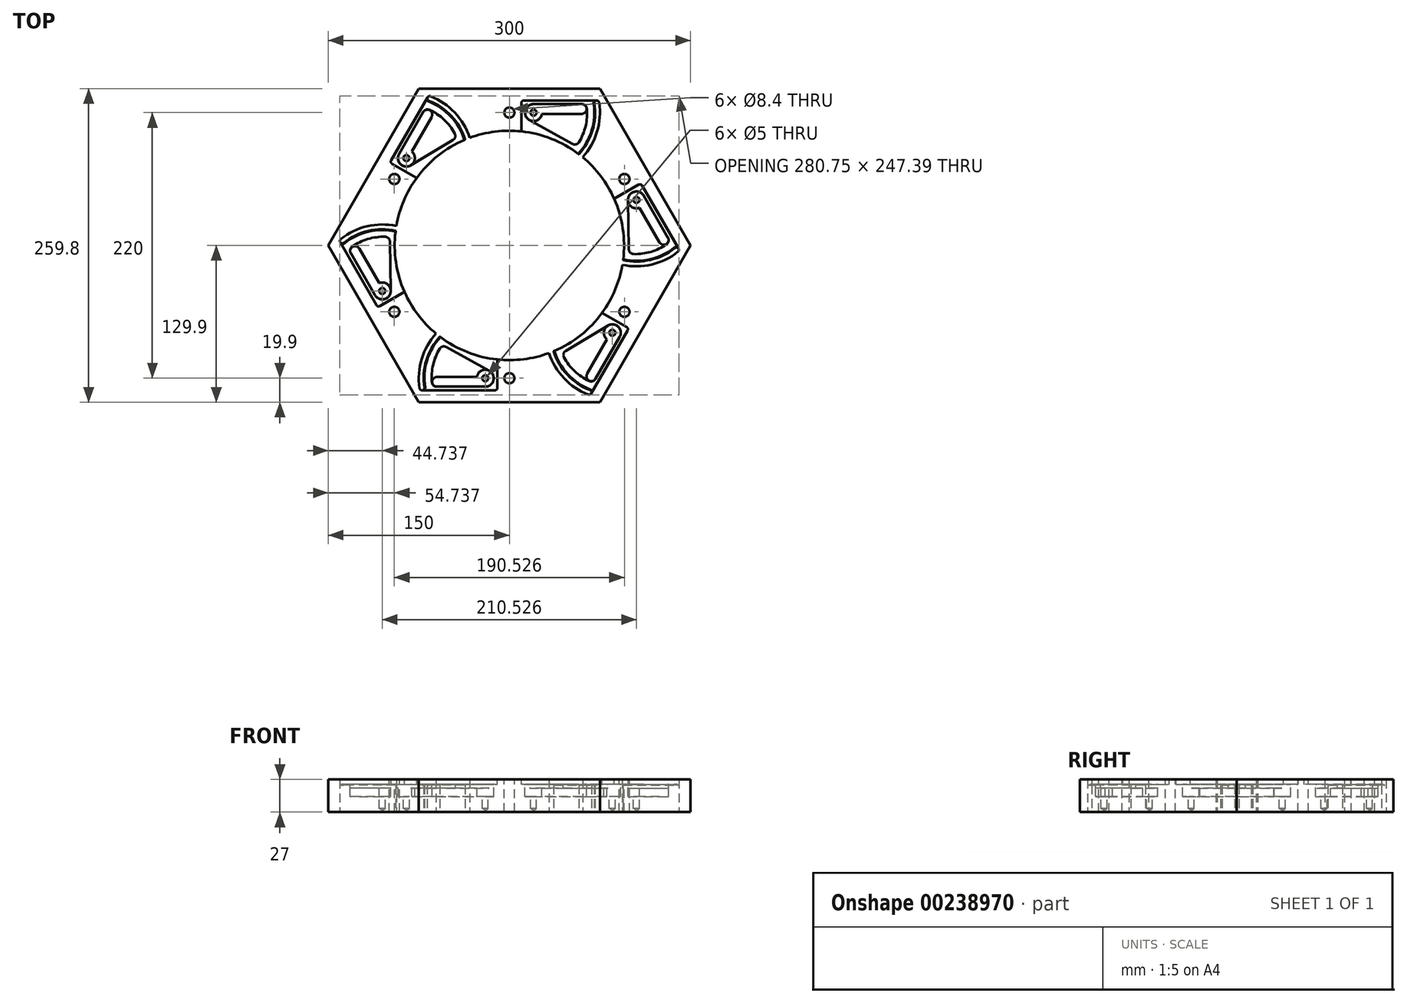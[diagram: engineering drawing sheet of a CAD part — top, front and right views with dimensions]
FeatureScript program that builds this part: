
annotation { "Feature Type Name" : "Feature", "Feature Type Description" : "" }
export const myFeature = defineFeature(function(context is Context, id is Id, definition is map)
    precondition{}
    {
        {
            var Q0;
            Q0=qCreatedBy(makeId("Top.planeOp"),FACE);
            var sketch = newSketch(context, id + "F0", { "sketchPlane" : qUnion([Q0])});
            skCircle(sketch, "E0.cCircle", {"center": v(0, 0) * mm, "radius": 150 * mm, "construction": true});
            skLineSegment(sketch, "E0.0", {"start": v(-75, 129.9) * mm, "end": v(75, 129.9) * mm});
            skLineSegment(sketch, "E0.1", {"start": v(75, 129.9) * mm, "end": v(150, 0) * mm});
            skLineSegment(sketch, "E0.2", {"start": v(150, 0) * mm, "end": v(75, -129.9) * mm});
            skLineSegment(sketch, "E0.3", {"start": v(75, -129.9) * mm, "end": v(-75, -129.9) * mm});
            skLineSegment(sketch, "E0.4", {"start": v(-75, -129.9) * mm, "end": v(-150, 0) * mm});
            skLineSegment(sketch, "E0.5", {"start": v(-150, 0) * mm, "end": v(-75, 129.9) * mm});
            skCircle(sketch, "E1", {"center": v(0, 0) * mm, "radius": 95 * mm});
            skLineSegment(sketch, "E2", {"start": v(0, -192.57) * mm, "end": v(0, 170.24) * mm, "construction": true});
            skCircle(sketch, "E3", {"center": v(0, 0) * mm, "radius": 110 * mm, "construction": true});
            skCircle(sketch, "E4", {"center": v(0, 110) * mm, "radius": 4.2 * mm});
            skCircle(sketch, "E5.1.0", {"center": v(-95.26, 55) * mm, "radius": 4.2 * mm});
            skCircle(sketch, "E5.2.0", {"center": v(-95.26, -55) * mm, "radius": 4.2 * mm});
            skCircle(sketch, "E5.3.0", {"center": v(0, -110) * mm, "radius": 4.2 * mm});
            skCircle(sketch, "E5.4.0", {"center": v(95.26, -55) * mm, "radius": 4.2 * mm});
            skCircle(sketch, "E5.5.0", {"center": v(95.26, 55) * mm, "radius": 4.2 * mm});
            skSolve(sketch);
        }
        {
            var Q0;
            Q0=qSketchRegion(id+"F0",true);
            extrude(context, id + "F1", {"entities" : qUnion([Q0]), "oppositeDirection" : true, "depth" : 25 * mm, "hasSecondDirection" : true, "secondDirectionOppositeDirection" : false, "secondDirectionDepth" : 2 * mm});
        }
        {
            var Q0;
            Q0=qCreatedBy(makeId("Top.planeOp"),FACE);
            var sketch = newSketch(context, id + "F2", { "sketchPlane" : qUnion([Q0])});
            skLineSegment(sketch, "E6", {"start": v(0, 0) * mm, "end": v(-115.33, 66.59) * mm, "construction": true});
            skLineSegment(sketch, "E7", {"start": v(24.73, 8.82) * mm, "end": v(-118.6, 91.57) * mm, "construction": true});
            skLineSegment(sketch, "E8", {"start": v(-73.53, 92.65) * mm, "end": v(-110.35, 28.87) * mm, "construction": true});
            skPoint(sketch, "E9", {"position": v(-85.26, 72.32) * mm});
            skArc(sketch, "E10", {"start": v(-79.2, 122.96) * mm, "mid": v(-97.67, 22.85) * mm, "end": v(-66.72, 119.83) * mm, "construction": true});
            skArc(sketch, "E11", {"start": v(-78.72, 126.93) * mm, "mid": v(-131.29, 42.21) * mm, "end": v(-32.6, 56.43) * mm});
            skCircle(sketch, "E12", {"center": v(-85.26, 72.32) * mm, "radius": 2.5 * mm, "construction": true});
            skArc(sketch, "E13", {"start": v(-86.7, 77.1) * mm, "mid": v(-89.8, 70.21) * mm, "end": v(-82.54, 68.13) * mm, "construction": true});
            skLineSegment(sketch, "E14", {"start": v(-95.36, 62.49) * mm, "end": v(-73.35, 109.7) * mm, "construction": true});
            skArc(sketch, "E15", {"start": v(-86.7, 77.1) * mm, "mid": v(-83.05, 79.12) * mm, "end": v(-80.54, 82.45) * mm, "construction": true});
            skLineSegment(sketch, "E16.trimOffspring", {"start": v(-80.54, 82.45) * mm, "end": v(-62.02, 122.17) * mm, "construction": true});
            skLineSegment(sketch, "E17.trimOffspring", {"start": v(-37.22, 89.44) * mm, "end": v(-33.46, 90.8) * mm});
            skPoint(sketch, "E18", {"position": v(-62.02, 122.17) * mm});
            skPoint(sketch, "E19", {"position": v(-33.46, 90.8) * mm});
            skArc(sketch, "E20", {"start": v(-37.22, 89.44) * mm, "mid": v(-37.91, 91.27) * mm, "end": v(-38.67, 93.07) * mm});
            skLineSegment(sketch, "E21", {"start": v(-82.54, 68.13) * mm, "end": v(-42.49, 94.14) * mm, "construction": true});
            skLineSegment(sketch, "E22", {"start": v(-50.7, 85.23) * mm, "end": v(-31.42, 97.75) * mm, "construction": true});
            skPoint(sketch, "E23", {"position": v(-39.97, 95.77) * mm});
            skCircle(sketch, "E24", {"center": v(-39.97, 95.77) * mm, "radius": 3 * mm, "construction": true});
            skPoint(sketch, "E25", {"position": v(-42.49, 94.14) * mm});
            skArc(sketch, "E26.trimOffspring", {"start": v(-39.97, 95.77) * mm, "mid": v(-49.96, 109.12) * mm, "end": v(-63.7, 118.54) * mm, "construction": true});
            skLineSegment(sketch, "E27.trimOffspring", {"start": v(-39.97, 95.77) * mm, "end": v(-16, 111.34) * mm});
            skArc(sketch, "E28", {"start": v(-38.67, 93.07) * mm, "mid": v(-40.33, 94.5) * mm, "end": v(-42.49, 94.14) * mm});
            skPoint(sketch, "E29", {"position": v(-77.2, 132.91) * mm});
            skPoint(sketch, "E30", {"position": v(-78.72, 126.93) * mm});
            skLineSegment(sketch, "E31", {"start": v(-85.26, 72.32) * mm, "end": v(-78.72, 126.93) * mm, "construction": true});
            skLineSegment(sketch, "E32", {"start": v(-85.21, 72.2) * mm, "end": v(-33.46, 90.8) * mm, "construction": true});
            skPoint(sketch, "E33", {"position": v(-56.33, 130.09) * mm});
            skLineSegment(sketch, "E34", {"start": v(-97.92, 70.4) * mm, "end": v(-67.73, 122.7) * mm});
            skLineSegment(sketch, "E35.1.0", {"start": v(0, 0) * mm, "end": v(-115.33, -66.59) * mm});
            skPoint(sketch, "E35.1.1", {"position": v(-105.26, -37.68) * mm});
            skLineSegment(sketch, "E35.2.0", {"start": v(0, 0) * mm, "end": v(0, -133.17) * mm});
            skPoint(sketch, "E35.2.1", {"position": v(-20, -110) * mm});
            skLineSegment(sketch, "E35.3.0", {"start": v(0, 0) * mm, "end": v(115.33, -66.59) * mm});
            skPoint(sketch, "E35.3.1", {"position": v(85.26, -72.32) * mm});
            skLineSegment(sketch, "E35.4.0", {"start": v(0, 0) * mm, "end": v(115.33, 66.59) * mm});
            skPoint(sketch, "E35.4.1", {"position": v(105.26, 37.68) * mm});
            skLineSegment(sketch, "E35.5.0", {"start": v(0, 0) * mm, "end": v(0, 133.17) * mm});
            skPoint(sketch, "E35.5.1", {"position": v(20, 110) * mm});
            skPoint(sketch, "E35.center", {"position": v(0, 0) * mm});
            skCircle(sketch, "E36.0", {"center": v(0, 0) * mm, "radius": 95 * mm, "construction": true});
            skPoint(sketch, "E37", {"position": v(-32.9, 89.12) * mm});
            skLineSegment(sketch, "E38", {"start": v(-32.9, 89.12) * mm, "end": v(32.9, -89.12) * mm, "construction": true});
            skPoint(sketch, "E39", {"position": v(-22.5, 60.98) * mm});
            skPoint(sketch, "E40", {"position": v(5.2, -14.07) * mm});
            skCircle(sketch, "E41", {"center": v(5.2, -14.07) * mm, "radius": 80 * mm, "construction": true});
            skArc(sketch, "E42.filletArc", {"start": v(-65.27, 123.56) * mm, "mid": v(-66.66, 123.58) * mm, "end": v(-67.73, 122.7) * mm});
            skLineSegment(sketch, "E43", {"start": v(-32.6, 56.43) * mm, "end": v(-85.26, 72.32) * mm, "construction": true});
            skLineSegment(sketch, "E44", {"start": v(-76.12, 72.3) * mm, "end": v(-85.21, 72.2) * mm});
            skLineSegment(sketch, "E45", {"start": v(-85.21, 72.2) * mm, "end": v(-56.33, 90.95) * mm, "construction": true});
            skLineSegment(sketch, "E46", {"start": v(-85.21, 72.2) * mm, "end": v(-48.78, 69.91) * mm, "construction": true});
            skLineSegment(sketch, "E47", {"start": v(-48.77, 65.04) * mm, "end": v(-92.23, 67.76) * mm, "construction": true});
            skCircle(sketch, "E48", {"center": v(-85.21, 72.2) * mm, "radius": 10 * mm, "construction": true});
            skLineSegment(sketch, "E49", {"start": v(-87.5, 62.45) * mm, "end": v(-55.32, 60.44) * mm, "construction": true});
            skLineSegment(sketch, "E50", {"start": v(-97.2, 67.66) * mm, "end": v(-68.1, 50.87) * mm});
            skArc(sketch, "E51.filletArc", {"start": v(-97.92, 70.4) * mm, "mid": v(-98.12, 68.87) * mm, "end": v(-97.2, 67.66) * mm});
            skArc(sketch, "E52", {"start": v(-67.73, 122.7) * mm, "mid": v(-67.88, 121.03) * mm, "end": v(-66.72, 119.83) * mm, "construction": true});
            skArc(sketch, "E53.converted", {"start": v(-30.7, 79.26) * mm, "mid": v(-41.9, 106.16) * mm, "end": v(-65.27, 123.56) * mm});
            skArc(sketch, "E54", {"start": v(-30.7, 79.26) * mm, "mid": v(-51.4, 67.7) * mm, "end": v(-68.1, 50.87) * mm});
            skLineSegment(sketch, "E55.trimOffspring", {"start": v(-52.18, 41.68) * mm, "end": v(-31.82, 29.92) * mm});
            skSolve(sketch);
        }
        {
            var Q0;
            Q0=qCreatedBy(makeId("Front.planeOp"),FACE);
            var sketch = newSketch(context, id + "F3", { "sketchPlane" : qUnion([Q0])});
            skLineSegment(sketch, "E56", {"start": v(0, -93.36) * mm, "end": v(0, 93) * mm, "construction": true});
            skSolve(sketch);
        }
        {
            var Q0;
            Q0=qSketchRegion(id+"F2",true);
            extrude(context, id + "F4", {"entities" : qUnion([Q0]), "depth" : 25 * mm, "hasSecondDirection" : true, "secondDirectionOppositeDirection" : true, "secondDirectionDepth" : 2.1 * mm});
        }
        {
            var Q0;
            Q0=makeQuery(id+"F4.opExtrude","SWEPT_BODY",BODY,{"disambiguationData":[OSD([sQuery(id+"F2.wireOp",EDGE,"E34"),sQuery(id+"F2.wireOp",EDGE,"E42.filletArc"),sQuery(id+"F2.wireOp",EDGE,"E50"),sQuery(id+"F2.wireOp",EDGE,"E51.filletArc"),sQuery(id+"F2.wireOp",EDGE,"E54"),sQuery(id+"F2.wireOp",EDGE,"E53.converted")])]});
            var Q1;
            Q1=sQuery(id+"F3.wireOp",EDGE,"E56");
            circularPattern(context, id + "F5", {"entities" : qUnion([Q0]), "axis" : qUnion([Q1]), "angle" : 360 * degree, "instanceCount" : 6, "equalSpace" : true});
        }
        {
            var Q0;
            Q0=makeQuery(id+"F5.opPattern","COPY",BODY,{"derivedFrom":makeQuery(id+"F4.opExtrude","SWEPT_BODY",BODY,{"disambiguationData":[OSD([sQuery(id+"F2.wireOp",EDGE,"E34"),sQuery(id+"F2.wireOp",EDGE,"E42.filletArc"),sQuery(id+"F2.wireOp",EDGE,"E50"),sQuery(id+"F2.wireOp",EDGE,"E51.filletArc"),sQuery(id+"F2.wireOp",EDGE,"E54"),sQuery(id+"F2.wireOp",EDGE,"E53.converted")])]}),"instanceName":"1"});
            var Q1;
            Q1=makeQuery(id+"F4.opExtrude","SWEPT_BODY",BODY,{"disambiguationData":[OSD([sQuery(id+"F2.wireOp",EDGE,"E34"),sQuery(id+"F2.wireOp",EDGE,"E42.filletArc"),sQuery(id+"F2.wireOp",EDGE,"E50"),sQuery(id+"F2.wireOp",EDGE,"E51.filletArc"),sQuery(id+"F2.wireOp",EDGE,"E54"),sQuery(id+"F2.wireOp",EDGE,"E53.converted")])]});
            var Q2;
            Q2=makeQuery(id+"F5.opPattern","COPY",BODY,{"derivedFrom":makeQuery(id+"F4.opExtrude","SWEPT_BODY",BODY,{"disambiguationData":[OSD([sQuery(id+"F2.wireOp",EDGE,"E34"),sQuery(id+"F2.wireOp",EDGE,"E42.filletArc"),sQuery(id+"F2.wireOp",EDGE,"E50"),sQuery(id+"F2.wireOp",EDGE,"E51.filletArc"),sQuery(id+"F2.wireOp",EDGE,"E54"),sQuery(id+"F2.wireOp",EDGE,"E53.converted")])]}),"instanceName":"5"});
            var Q3;
            Q3=makeQuery(id+"F5.opPattern","COPY",BODY,{"derivedFrom":makeQuery(id+"F4.opExtrude","SWEPT_BODY",BODY,{"disambiguationData":[OSD([sQuery(id+"F2.wireOp",EDGE,"E34"),sQuery(id+"F2.wireOp",EDGE,"E42.filletArc"),sQuery(id+"F2.wireOp",EDGE,"E50"),sQuery(id+"F2.wireOp",EDGE,"E51.filletArc"),sQuery(id+"F2.wireOp",EDGE,"E54"),sQuery(id+"F2.wireOp",EDGE,"E53.converted")])]}),"instanceName":"4"});
            var Q4;
            Q4=makeQuery(id+"F5.opPattern","COPY",BODY,{"derivedFrom":makeQuery(id+"F4.opExtrude","SWEPT_BODY",BODY,{"disambiguationData":[OSD([sQuery(id+"F2.wireOp",EDGE,"E34"),sQuery(id+"F2.wireOp",EDGE,"E42.filletArc"),sQuery(id+"F2.wireOp",EDGE,"E50"),sQuery(id+"F2.wireOp",EDGE,"E51.filletArc"),sQuery(id+"F2.wireOp",EDGE,"E54"),sQuery(id+"F2.wireOp",EDGE,"E53.converted")])]}),"instanceName":"3"});
            var Q5;
            Q5=makeQuery(id+"F5.opPattern","COPY",BODY,{"derivedFrom":makeQuery(id+"F4.opExtrude","SWEPT_BODY",BODY,{"disambiguationData":[OSD([sQuery(id+"F2.wireOp",EDGE,"E34"),sQuery(id+"F2.wireOp",EDGE,"E42.filletArc"),sQuery(id+"F2.wireOp",EDGE,"E50"),sQuery(id+"F2.wireOp",EDGE,"E51.filletArc"),sQuery(id+"F2.wireOp",EDGE,"E54"),sQuery(id+"F2.wireOp",EDGE,"E53.converted")])]}),"instanceName":"2"});
            var Q6;
            Q6=makeQuery(id+"F1.opExtrude","SWEPT_BODY",BODY,{"disambiguationData":[OSD([sQuery(id+"F0.wireOp",EDGE,"E0.0"),sQuery(id+"F0.wireOp",EDGE,"E0.1"),sQuery(id+"F0.wireOp",EDGE,"E0.2"),sQuery(id+"F0.wireOp",EDGE,"E0.3"),sQuery(id+"F0.wireOp",EDGE,"E0.4"),sQuery(id+"F0.wireOp",EDGE,"E0.5"),sQuery(id+"F0.wireOp",EDGE,"E1")])]});
            booleanBodies(context, id + "F6", {"operationType" : BooleanOperationType.SUBTRACTION, "tools" : qUnion([Q0, Q1, Q2, Q3, Q4, Q5]), "targets" : qUnion([Q6])});
        }
        {
            var Q0;
            Q0=makeQuery(id+"F0.imprint","IMPRINT",FACE,{"disambiguationData":[TD([[makeQuery(id+"F0.imprint","IMPRINT",EDGE,{"derivedFrom":sQuery(id+"F0.wireOp",EDGE,"E1")}),1.0]])]});
            var sketch = newSketch(context, id + "F7", { "sketchPlane" : qUnion([Q0])});
            skArc(sketch, "E57.1", {"start": v(-34.54, 77.66) * mm, "mid": v(-44.72, 103.26) * mm, "end": v(-66.72, 119.83) * mm});
            skArc(sketch, "E58.0", {"start": v(-30.7, 79.26) * mm, "mid": v(-32.63, 78.49) * mm, "end": v(-34.54, 77.66) * mm});
            skArc(sketch, "E59.0", {"start": v(-67.73, 122.7) * mm, "mid": v(-67.88, 121.03) * mm, "end": v(-66.72, 119.83) * mm});
            skArc(sketch, "E59.1", {"start": v(-65.27, 123.56) * mm, "mid": v(-66.66, 123.58) * mm, "end": v(-67.73, 122.7) * mm});
            skArc(sketch, "E59.2", {"start": v(-30.7, 79.26) * mm, "mid": v(-41.9, 106.16) * mm, "end": v(-65.27, 123.56) * mm});
            skPoint(sketch, "E60.orphan", {"position": v(-68.1, 50.87) * mm});
            skPoint(sketch, "E61.orphan", {"position": v(-79.2, 122.96) * mm});
            skPoint(sketch, "E57.0.end.orphan", {"position": v(-97.92, 70.4) * mm});
            skPoint(sketch, "E57.0.start.orphan", {"position": v(-67.73, 122.7) * mm});
            skSolve(sketch);
        }
        {
            var Q0;
            Q0=qSketchRegion(id+"F7",true);
            extrude(context, id + "F8", {"entities" : qUnion([Q0]), "depth" : 10 * mm, "hasSecondDirection" : true, "secondDirectionOppositeDirection" : true, "secondDirectionDepth" : 35 * mm});
        }
        {
            var Q0;
            Q0=makeQuery(id+"F8.opExtrude","SWEPT_BODY",BODY,{"disambiguationData":[OSD([sQuery(id+"F7.wireOp",EDGE,"E57.1"),sQuery(id+"F7.wireOp",EDGE,"E58.0"),sQuery(id+"F7.wireOp",EDGE,"E59.0"),sQuery(id+"F7.wireOp",EDGE,"E59.1"),sQuery(id+"F7.wireOp",EDGE,"E59.2")])]});
            var Q1;
            Q1=sQuery(id+"F3.wireOp",EDGE,"E56");
            circularPattern(context, id + "F9", {"entities" : qUnion([Q0]), "axis" : qUnion([Q1]), "angle" : 360 * degree, "instanceCount" : 6, "equalSpace" : true});
        }
        {
            var Q0;
            Q0=makeQuery(id+"F8.opExtrude","SWEPT_BODY",BODY,{"disambiguationData":[OSD([sQuery(id+"F7.wireOp",EDGE,"E57.1"),sQuery(id+"F7.wireOp",EDGE,"E58.0"),sQuery(id+"F7.wireOp",EDGE,"E59.0"),sQuery(id+"F7.wireOp",EDGE,"E59.1"),sQuery(id+"F7.wireOp",EDGE,"E59.2")])]});
            var Q1;
            Q1=makeQuery(id+"F9.opPattern","COPY",BODY,{"derivedFrom":makeQuery(id+"F8.opExtrude","SWEPT_BODY",BODY,{"disambiguationData":[OSD([sQuery(id+"F7.wireOp",EDGE,"E57.1"),sQuery(id+"F7.wireOp",EDGE,"E58.0"),sQuery(id+"F7.wireOp",EDGE,"E59.0"),sQuery(id+"F7.wireOp",EDGE,"E59.1"),sQuery(id+"F7.wireOp",EDGE,"E59.2")])]}),"instanceName":"5"});
            var Q2;
            Q2=makeQuery(id+"F9.opPattern","COPY",BODY,{"derivedFrom":makeQuery(id+"F8.opExtrude","SWEPT_BODY",BODY,{"disambiguationData":[OSD([sQuery(id+"F7.wireOp",EDGE,"E57.1"),sQuery(id+"F7.wireOp",EDGE,"E58.0"),sQuery(id+"F7.wireOp",EDGE,"E59.0"),sQuery(id+"F7.wireOp",EDGE,"E59.1"),sQuery(id+"F7.wireOp",EDGE,"E59.2")])]}),"instanceName":"4"});
            var Q3;
            Q3=makeQuery(id+"F9.opPattern","COPY",BODY,{"derivedFrom":makeQuery(id+"F8.opExtrude","SWEPT_BODY",BODY,{"disambiguationData":[OSD([sQuery(id+"F7.wireOp",EDGE,"E57.1"),sQuery(id+"F7.wireOp",EDGE,"E58.0"),sQuery(id+"F7.wireOp",EDGE,"E59.0"),sQuery(id+"F7.wireOp",EDGE,"E59.1"),sQuery(id+"F7.wireOp",EDGE,"E59.2")])]}),"instanceName":"3"});
            var Q4;
            Q4=makeQuery(id+"F9.opPattern","COPY",BODY,{"derivedFrom":makeQuery(id+"F8.opExtrude","SWEPT_BODY",BODY,{"disambiguationData":[OSD([sQuery(id+"F7.wireOp",EDGE,"E57.1"),sQuery(id+"F7.wireOp",EDGE,"E58.0"),sQuery(id+"F7.wireOp",EDGE,"E59.0"),sQuery(id+"F7.wireOp",EDGE,"E59.1"),sQuery(id+"F7.wireOp",EDGE,"E59.2")])]}),"instanceName":"2"});
            var Q5;
            Q5=makeQuery(id+"F9.opPattern","COPY",BODY,{"derivedFrom":makeQuery(id+"F8.opExtrude","SWEPT_BODY",BODY,{"disambiguationData":[OSD([sQuery(id+"F7.wireOp",EDGE,"E57.1"),sQuery(id+"F7.wireOp",EDGE,"E58.0"),sQuery(id+"F7.wireOp",EDGE,"E59.0"),sQuery(id+"F7.wireOp",EDGE,"E59.1"),sQuery(id+"F7.wireOp",EDGE,"E59.2")])]}),"instanceName":"1"});
            var Q6;
            Q6=makeQuery(id+"F1.opExtrude","SWEPT_BODY",BODY,{"disambiguationData":[OSD([sQuery(id+"F0.wireOp",EDGE,"E0.0"),sQuery(id+"F0.wireOp",EDGE,"E0.1"),sQuery(id+"F0.wireOp",EDGE,"E0.2"),sQuery(id+"F0.wireOp",EDGE,"E0.3"),sQuery(id+"F0.wireOp",EDGE,"E0.4"),sQuery(id+"F0.wireOp",EDGE,"E0.5"),sQuery(id+"F0.wireOp",EDGE,"E1")])]});
            booleanBodies(context, id + "F10", {"operationType" : BooleanOperationType.SUBTRACTION, "tools" : qUnion([Q0, Q1, Q2, Q3, Q4, Q5]), "targets" : qUnion([Q6])});
        }
        {
            var Q0;
            Q0=sQuery(id+"F2.wireOp",VERTEX,"E35.5.1");
            var Q1;
            Q1=sQuery(id+"F2.wireOp",VERTEX,"E35.4.1");
            var Q2;
            Q2=sQuery(id+"F2.wireOp",VERTEX,"E35.3.1");
            var Q3;
            Q3=sQuery(id+"F2.wireOp",VERTEX,"E35.2.1");
            var Q4;
            Q4=sQuery(id+"F2.wireOp",VERTEX,"E35.1.1");
            var Q5;
            Q5=sQuery(id+"F2.wireOp",VERTEX,"E9");
            var Q6;
            Q6=makeQuery(id+"F1.opExtrude","SWEPT_BODY",BODY,{"disambiguationData":[OSD([sQuery(id+"F0.wireOp",EDGE,"E0.0"),sQuery(id+"F0.wireOp",EDGE,"E0.1"),sQuery(id+"F0.wireOp",EDGE,"E0.2"),sQuery(id+"F0.wireOp",EDGE,"E0.3"),sQuery(id+"F0.wireOp",EDGE,"E0.4"),sQuery(id+"F0.wireOp",EDGE,"E0.5"),sQuery(id+"F0.wireOp",EDGE,"E1")])]});
            hole(context, id + "F11", {"style" : HoleStyle.SIMPLE, "endStyle" : HoleEndStyle.BLIND, "holeDiameter" : 5 * mm, "holeDepth" : 20 * mm, "locations" : qUnion([Q0, Q1, Q2, Q3, Q4, Q5]), "scope" : qUnion([Q6])});
        }
        {
            var Q0;
            Q0=makeQuery(id+"F6.opBoolean","COPY",FACE,{"derivedFrom":makeQuery(id+"F4.opExtrude","CAP_FACE",FACE,{"disambiguationData":[OSD([sQuery(id+"F2.wireOp",EDGE,"E34"),sQuery(id+"F2.wireOp",EDGE,"E42.filletArc"),sQuery(id+"F2.wireOp",EDGE,"E50"),sQuery(id+"F2.wireOp",EDGE,"E51.filletArc"),sQuery(id+"F2.wireOp",EDGE,"E54"),sQuery(id+"F2.wireOp",EDGE,"E53.converted")])],"isStart":true})});
            cPlane(context, id + "F12", {"entities" : qUnion([Q0]), "cplaneType" : CPlaneType.OFFSET, "offset" : 0 * mm, "width" : 150 * mm, "height" : 150 * mm});
        }
        {
            var Q0;
            Q0=qCreatedBy(id+"F12.planeOp",FACE);
            var sketch = newSketch(context, id + "F13", { "sketchPlane" : qUnion([Q0])});
            skCircle(sketch, "E62.0", {"center": v(-85.26, 72.32) * mm, "radius": 7 * mm});
            skLineSegment(sketch, "E63", {"start": v(-91.32, 75.82) * mm, "end": v(-67.64, 116.85) * mm});
            skLineSegment(sketch, "E64", {"start": v(-87.86, 73.82) * mm, "end": v(-63.58, 115.87) * mm, "construction": true});
            skLineSegment(sketch, "E65", {"start": v(-91.32, 75.82) * mm, "end": v(-76.61, 67.33) * mm, "construction": true});
            skLineSegment(sketch, "E66", {"start": v(-77.1, 113.8) * mm, "end": v(-55.5, 101.33) * mm, "construction": true});
            skArc(sketch, "E67", {"start": v(-64.4, 106.46) * mm, "mid": v(-65.86, 111.93) * mm, "end": v(-71.32, 110.46) * mm});
            skArc(sketch, "E68", {"start": v(-91.32, 75.82) * mm, "mid": v(-89.86, 70.36) * mm, "end": v(-84.4, 71.82) * mm});
            skLineSegment(sketch, "E69", {"start": v(-64.4, 106.46) * mm, "end": v(-84.4, 71.82) * mm});
            skSolve(sketch);
        }
        {
            var Q0;
            Q0 = qSketchRegion(id + "F13", true);
            extrude(context, id + "F14", {"entities" : qUnion([Q0]), "oppositeDirection" : true, "depth" : 10 * mm, "hasSecondDirection" : true, "secondDirectionOppositeDirection" : false, "secondDirectionDepth" : 25 * mm});
        }
        {
            var Q0;
            Q0=makeQuery(id+"F14.opExtrude","SWEPT_BODY",BODY,{"disambiguationData":[OSD([sQuery(id+"F13.wireOp",EDGE,"E62.0")])]});
            var Q1;
            Q1=sQuery(id+"F3.wireOp",EDGE,"E56");
            circularPattern(context, id + "F15", {"operationType" : NewBodyOperationType.REMOVE, "entities" : qUnion([Q0]), "axis" : qUnion([Q1]), "angle" : 360 * degree, "instanceCount" : 6, "equalSpace" : true});
        }
        {
            var Q0;
            Q0=qCreatedBy(id+"F12.planeOp",FACE);
            var sketch = newSketch(context, id + "F16", { "sketchPlane" : qUnion([Q0])});
            skArc(sketch, "E70.0", {"start": v(-66.31, 118.88) * mm, "mid": v(-47.6, 106.21) * mm, "end": v(-36.21, 86.7) * mm, "construction": true});
            skCircle(sketch, "E71.0", {"center": v(-85.26, 72.32) * mm, "radius": 4.5 * mm, "construction": true});
            skLineSegment(sketch, "E72.0", {"start": v(-67.73, 122.7) * mm, "end": v(-103.72, 60.35) * mm, "construction": true});
            skArc(sketch, "E73.0", {"start": v(-76.82, 55.9) * mm, "mid": v(-58.9, 74.54) * mm, "end": v(-36.62, 87.66) * mm, "construction": true});
            skArc(sketch, "E74", {"start": v(-45.23, 92.65) * mm, "mid": v(-54.06, 104.16) * mm, "end": v(-66.1, 112.27) * mm});
            skPoint(sketch, "E75.orphan", {"position": v(-61.95, 122.7) * mm});
            skArc(sketch, "E76.0.0", {"start": v(-91.32, 75.82) * mm, "mid": v(-90.17, 67.33) * mm, "end": v(-81.66, 66.32) * mm});
            skLineSegment(sketch, "E77", {"start": v(-91.32, 75.82) * mm, "end": v(-71.23, 110.63) * mm});
            skLineSegment(sketch, "E78", {"start": v(-46.7, 87.33) * mm, "end": v(-81.66, 66.32) * mm});
            skPoint(sketch, "E79.visualSharp", {"position": v(-69.48, 113.66) * mm});
            skArc(sketch, "E79.filletArc", {"start": v(-66.1, 112.27) * mm, "mid": v(-68.97, 112.45) * mm, "end": v(-71.23, 110.63) * mm});
            skPoint(sketch, "E80.visualSharp", {"position": v(-43.57, 89.2) * mm});
            skArc(sketch, "E80.filletArc", {"start": v(-46.7, 87.33) * mm, "mid": v(-44.9, 89.7) * mm, "end": v(-45.23, 92.65) * mm});
            skSolve(sketch);
        }
        {
            var Q0;
            Q0 = qSketchRegion(id + "F16", true);
            extrude(context, id + "F17", {"entities" : qUnion([Q0]), "oppositeDirection" : true, "depth" : 3 * mm, "hasSecondDirection" : true, "secondDirectionOppositeDirection" : false, "secondDirectionDepth" : 25 * mm});
        }
        {
            var Q0;
            Q0=makeQuery(id+"F17.opExtrude","SWEPT_BODY",BODY,{"disambiguationData":[OSD([sQuery(id+"F16.wireOp",EDGE,"E74"),sQuery(id+"F16.wireOp",EDGE,"E76.0.0"),sQuery(id+"F16.wireOp",EDGE,"E77"),sQuery(id+"F16.wireOp",EDGE,"E78"),sQuery(id+"F16.wireOp",EDGE,"E79.filletArc"),sQuery(id+"F16.wireOp",EDGE,"E80.filletArc")])]});
            var Q1;
            Q1=sQuery(id+"F3.wireOp",EDGE,"E56");
            circularPattern(context, id + "F18", {"operationType" : NewBodyOperationType.REMOVE, "entities" : qUnion([Q0]), "axis" : qUnion([Q1]), "angle" : 360 * degree, "instanceCount" : 6, "oppositeDirection" : true, "equalSpace" : true});
        }
        {
            var Q0;
            Q0=makeQuery(id+"F10.opBoolean","INTERSECT",EDGE,{"derivedFrom":[makeQuery(id+"F6.opBoolean","COPY",FACE,{"derivedFrom":makeQuery(id+"F5.opPattern","COPY",FACE,{"derivedFrom":makeQuery(id+"F4.opExtrude","CAP_FACE",FACE,{"disambiguationData":[OSD([sQuery(id+"F2.wireOp",EDGE,"E34"),sQuery(id+"F2.wireOp",EDGE,"E42.filletArc"),sQuery(id+"F2.wireOp",EDGE,"E50"),sQuery(id+"F2.wireOp",EDGE,"E51.filletArc"),sQuery(id+"F2.wireOp",EDGE,"E54"),sQuery(id+"F2.wireOp",EDGE,"E53.converted")])],"isStart":true}),"instanceName":"1"})}),makeQuery(id+"F9.opPattern","COPY",FACE,{"derivedFrom":makeQuery(id+"F8.opExtrude","SWEPT_FACE",FACE,{"disambiguationData":[OSD([sQuery(id+"F7.wireOp",EDGE,"E57.1")])]}),"instanceName":"1"})]});
            var Q1;
            Q1=makeQuery(id+"F10.opBoolean","INTERSECT",EDGE,{"derivedFrom":[makeQuery(id+"F6.opBoolean","COPY",FACE,{"derivedFrom":makeQuery(id+"F4.opExtrude","CAP_FACE",FACE,{"disambiguationData":[OSD([sQuery(id+"F2.wireOp",EDGE,"E34"),sQuery(id+"F2.wireOp",EDGE,"E42.filletArc"),sQuery(id+"F2.wireOp",EDGE,"E50"),sQuery(id+"F2.wireOp",EDGE,"E51.filletArc"),sQuery(id+"F2.wireOp",EDGE,"E54"),sQuery(id+"F2.wireOp",EDGE,"E53.converted")])],"isStart":true})}),makeQuery(id+"F8.opExtrude","SWEPT_FACE",FACE,{"disambiguationData":[OSD([sQuery(id+"F7.wireOp",EDGE,"E57.1")])]})]});
            var Q2;
            Q2=makeQuery(id+"F10.opBoolean","INTERSECT",EDGE,{"derivedFrom":[makeQuery(id+"F6.opBoolean","COPY",FACE,{"derivedFrom":makeQuery(id+"F5.opPattern","COPY",FACE,{"derivedFrom":makeQuery(id+"F4.opExtrude","CAP_FACE",FACE,{"disambiguationData":[OSD([sQuery(id+"F2.wireOp",EDGE,"E34"),sQuery(id+"F2.wireOp",EDGE,"E42.filletArc"),sQuery(id+"F2.wireOp",EDGE,"E50"),sQuery(id+"F2.wireOp",EDGE,"E51.filletArc"),sQuery(id+"F2.wireOp",EDGE,"E54"),sQuery(id+"F2.wireOp",EDGE,"E53.converted")])],"isStart":true}),"instanceName":"5"})}),makeQuery(id+"F9.opPattern","COPY",FACE,{"derivedFrom":makeQuery(id+"F8.opExtrude","SWEPT_FACE",FACE,{"disambiguationData":[OSD([sQuery(id+"F7.wireOp",EDGE,"E57.1")])]}),"instanceName":"5"})]});
            var Q3;
            Q3=makeQuery(id+"F10.opBoolean","INTERSECT",EDGE,{"derivedFrom":[makeQuery(id+"F6.opBoolean","COPY",FACE,{"derivedFrom":makeQuery(id+"F5.opPattern","COPY",FACE,{"derivedFrom":makeQuery(id+"F4.opExtrude","CAP_FACE",FACE,{"disambiguationData":[OSD([sQuery(id+"F2.wireOp",EDGE,"E34"),sQuery(id+"F2.wireOp",EDGE,"E42.filletArc"),sQuery(id+"F2.wireOp",EDGE,"E50"),sQuery(id+"F2.wireOp",EDGE,"E51.filletArc"),sQuery(id+"F2.wireOp",EDGE,"E54"),sQuery(id+"F2.wireOp",EDGE,"E53.converted")])],"isStart":true}),"instanceName":"4"})}),makeQuery(id+"F9.opPattern","COPY",FACE,{"derivedFrom":makeQuery(id+"F8.opExtrude","SWEPT_FACE",FACE,{"disambiguationData":[OSD([sQuery(id+"F7.wireOp",EDGE,"E57.1")])]}),"instanceName":"4"})]});
            var Q4;
            Q4=makeQuery(id+"F10.opBoolean","INTERSECT",EDGE,{"derivedFrom":[makeQuery(id+"F6.opBoolean","COPY",FACE,{"derivedFrom":makeQuery(id+"F5.opPattern","COPY",FACE,{"derivedFrom":makeQuery(id+"F4.opExtrude","CAP_FACE",FACE,{"disambiguationData":[OSD([sQuery(id+"F2.wireOp",EDGE,"E34"),sQuery(id+"F2.wireOp",EDGE,"E42.filletArc"),sQuery(id+"F2.wireOp",EDGE,"E50"),sQuery(id+"F2.wireOp",EDGE,"E51.filletArc"),sQuery(id+"F2.wireOp",EDGE,"E54"),sQuery(id+"F2.wireOp",EDGE,"E53.converted")])],"isStart":true}),"instanceName":"3"})}),makeQuery(id+"F9.opPattern","COPY",FACE,{"derivedFrom":makeQuery(id+"F8.opExtrude","SWEPT_FACE",FACE,{"disambiguationData":[OSD([sQuery(id+"F7.wireOp",EDGE,"E57.1")])]}),"instanceName":"3"})]});
            var Q5;
            Q5=makeQuery(id+"F10.opBoolean","INTERSECT",EDGE,{"derivedFrom":[makeQuery(id+"F6.opBoolean","COPY",FACE,{"derivedFrom":makeQuery(id+"F5.opPattern","COPY",FACE,{"derivedFrom":makeQuery(id+"F4.opExtrude","CAP_FACE",FACE,{"disambiguationData":[OSD([sQuery(id+"F2.wireOp",EDGE,"E34"),sQuery(id+"F2.wireOp",EDGE,"E42.filletArc"),sQuery(id+"F2.wireOp",EDGE,"E50"),sQuery(id+"F2.wireOp",EDGE,"E51.filletArc"),sQuery(id+"F2.wireOp",EDGE,"E54"),sQuery(id+"F2.wireOp",EDGE,"E53.converted")])],"isStart":true}),"instanceName":"2"})}),makeQuery(id+"F9.opPattern","COPY",FACE,{"derivedFrom":makeQuery(id+"F8.opExtrude","SWEPT_FACE",FACE,{"disambiguationData":[OSD([sQuery(id+"F7.wireOp",EDGE,"E57.1")])]}),"instanceName":"2"})]});
            chamfer(context, id + "F19", {"entities" : qUnion([Q0, Q1, Q2, Q3, Q4, Q5]), "width" : 0.6 * mm, "tangentPropagation" : true});
        }
    });
